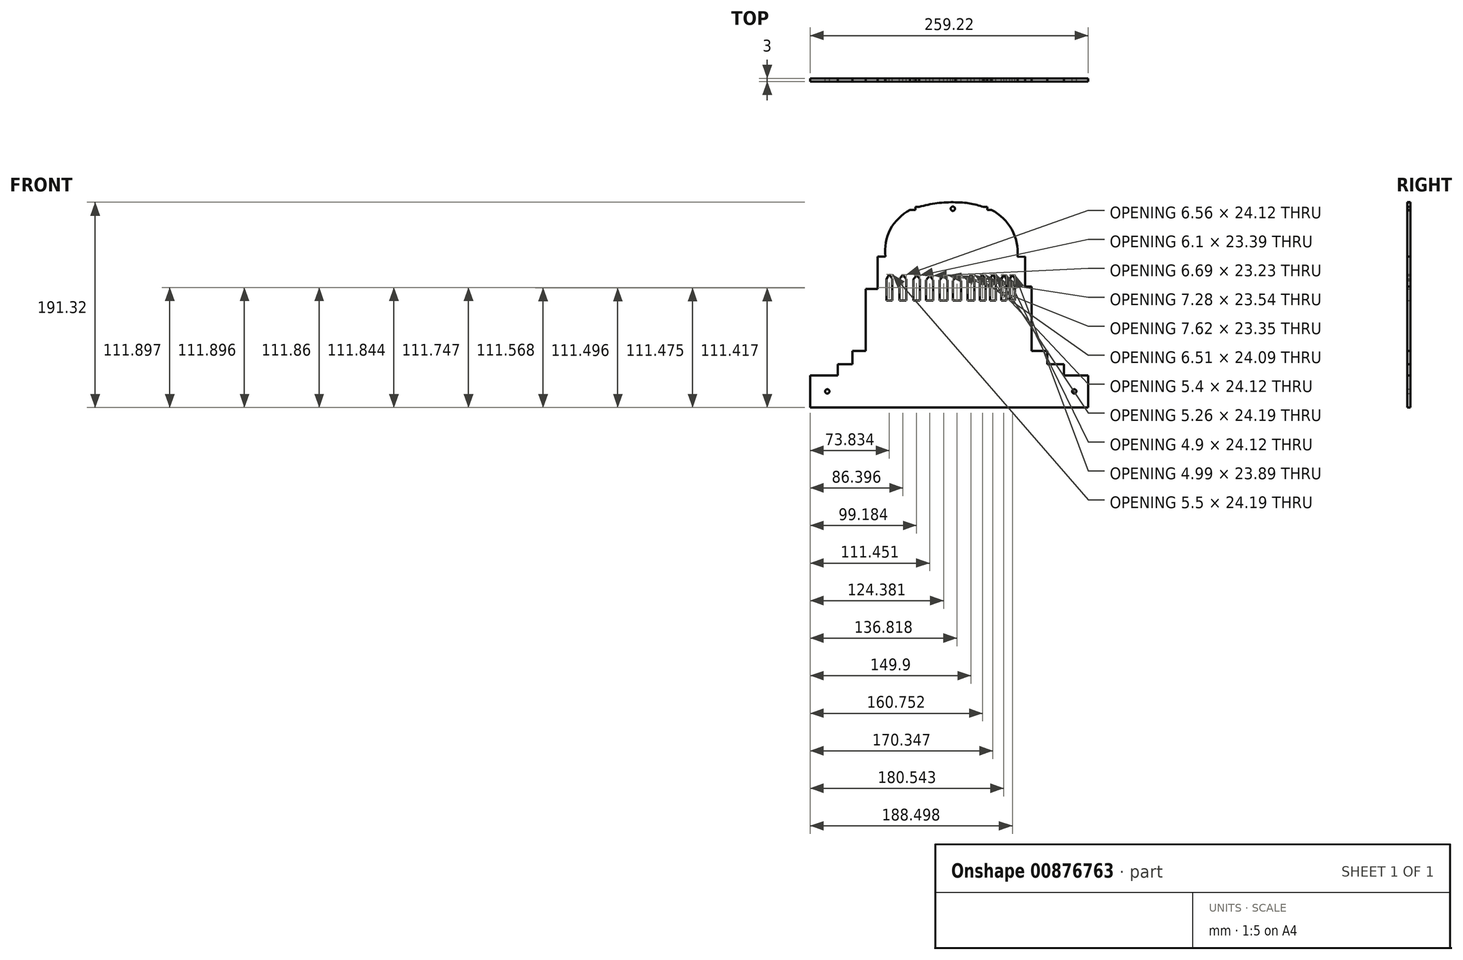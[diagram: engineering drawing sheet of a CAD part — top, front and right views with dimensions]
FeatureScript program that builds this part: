
annotation { "Feature Type Name" : "Feature", "Feature Type Description" : "" }
export const myFeature = defineFeature(function(context is Context, id is Id, definition is map)
    precondition{}
    {
        {
            var Q0;
            Q0=qCreatedBy(makeId("Front.planeOp"),FACE);
            var sketch = newSketch(context, id + "F0", { "sketchPlane" : qUnion([Q0])});
            skLineSegment(sketch, "E0.bottom", {"start": v(-192.48, 145.91) * mm, "end": v(107.52, 145.91) * mm});
            skLineSegment(sketch, "E0.top", {"start": v(-192.48, -54.09) * mm, "end": v(107.52, -54.09) * mm});
            skLineSegment(sketch, "E0.left", {"start": v(-192.48, 145.91) * mm, "end": v(-192.48, -54.09) * mm});
            skLineSegment(sketch, "E0.right", {"start": v(107.52, 145.91) * mm, "end": v(107.52, -54.09) * mm});
            skLineSegment(sketch, "E1.bottom", {"start": v(-179.38, -19.27) * mm, "end": v(79.84, -19.27) * mm});
            skLineSegment(sketch, "E1.top", {"start": v(-179.38, -49.27) * mm, "end": v(79.84, -49.27) * mm});
            skLineSegment(sketch, "E1.left", {"start": v(-179.38, -19.27) * mm, "end": v(-179.38, -49.27) * mm});
            skLineSegment(sketch, "E1.right", {"start": v(79.84, -19.27) * mm, "end": v(79.84, -49.27) * mm});
            skLineSegment(sketch, "E2", {"start": v(-153.49, -19.27) * mm, "end": v(-153.49, -9.07) * mm});
            skLineSegment(sketch, "E3", {"start": v(-153.49, -9.07) * mm, "end": v(57.28, -9.07) * mm});
            skLineSegment(sketch, "E4", {"start": v(57.28, -9.07) * mm, "end": v(57.28, -19.27) * mm});
            skLineSegment(sketch, "E5", {"start": v(-139.9, -9.07) * mm, "end": v(-139.9, 3.53) * mm});
            skLineSegment(sketch, "E6", {"start": v(-139.9, 3.53) * mm, "end": v(41.53, 3.53) * mm});
            skLineSegment(sketch, "E7", {"start": v(41.53, 3.53) * mm, "end": v(41.53, -9.07) * mm});
            skLineSegment(sketch, "E8", {"start": v(27.04, 3.53) * mm, "end": v(27.04, 63.53) * mm});
            skLineSegment(sketch, "E9", {"start": v(-127.6, 3.53) * mm, "end": v(-127.6, 61.2) * mm});
            skLineSegment(sketch, "E10", {"start": v(27.04, 63.53) * mm, "end": v(21.03, 63.53) * mm});
            skLineSegment(sketch, "E11", {"start": v(21.03, 63.53) * mm, "end": v(21.03, 91.26) * mm});
            skLineSegment(sketch, "E12", {"start": v(-116.37, 61.2) * mm, "end": v(-116.37, 91.36) * mm});
            skLineSegment(sketch, "E13", {"start": v(-116.37, 91.36) * mm, "end": v(-109.23, 91.36) * mm});
            skLineSegment(sketch, "E14", {"start": v(-108.3, 50.53) * mm, "end": v(15.5, 50.53) * mm});
            skLineSegment(sketch, "E15", {"start": v(-99.12, 50.53) * mm, "end": v(-99.12, 50.53) * mm});
            skLineSegment(sketch, "E16", {"start": v(-96.27, 50.53) * mm, "end": v(-96.27, 70.4) * mm});
            skLineSegment(sketch, "E17", {"start": v(-89.7, 70.4) * mm, "end": v(-89.7, 50.53) * mm});
            skLineSegment(sketch, "E18", {"start": v(-83.24, 50.53) * mm, "end": v(-83.24, 70.42) * mm});
            skLineSegment(sketch, "E19", {"start": v(-83.24, 70.42) * mm, "end": v(-79.9, 73.92) * mm});
            skLineSegment(sketch, "E20", {"start": v(-79.9, 73.92) * mm, "end": v(-77.15, 70.42) * mm});
            skLineSegment(sketch, "E21", {"start": v(-77.15, 70.42) * mm, "end": v(-77.15, 50.53) * mm});
            skLineSegment(sketch, "E22", {"start": v(-71.27, 50.53) * mm, "end": v(-71.27, 69.55) * mm});
            skLineSegment(sketch, "E23", {"start": v(-71.27, 69.55) * mm, "end": v(-67.9, 73.76) * mm});
            skLineSegment(sketch, "E24", {"start": v(-67.9, 73.76) * mm, "end": v(-64.59, 69.55) * mm});
            skLineSegment(sketch, "E25", {"start": v(-64.59, 69.55) * mm, "end": v(-64.59, 50.53) * mm});
            skLineSegment(sketch, "E26", {"start": v(-58.64, 50.53) * mm, "end": v(-58.64, 69.34) * mm});
            skLineSegment(sketch, "E27", {"start": v(-58.64, 69.34) * mm, "end": v(-54.86, 74.07) * mm});
            skLineSegment(sketch, "E28", {"start": v(-54.86, 74.07) * mm, "end": v(-51.36, 69.34) * mm});
            skLineSegment(sketch, "E29", {"start": v(-51.36, 69.34) * mm, "end": v(-51.36, 50.53) * mm});
            skPoint(sketch, "E30", {"position": v(-54.86, 78.15) * mm});
            skLineSegment(sketch, "E31", {"start": v(-46.37, 50.53) * mm, "end": v(-46.37, 68.7) * mm});
            skLineSegment(sketch, "E32", {"start": v(-46.37, 68.7) * mm, "end": v(-42.4, 73.88) * mm});
            skLineSegment(sketch, "E33", {"start": v(-42.4, 73.88) * mm, "end": v(-38.75, 68.7) * mm});
            skLineSegment(sketch, "E34", {"start": v(-38.75, 68.7) * mm, "end": v(-38.75, 50.53) * mm});
            skLineSegment(sketch, "E35", {"start": v(-32.74, 50.53) * mm, "end": v(-32.74, 69.57) * mm});
            skLineSegment(sketch, "E36", {"start": v(-32.74, 69.57) * mm, "end": v(-29.58, 74.62) * mm});
            skLineSegment(sketch, "E37", {"start": v(-29.58, 74.62) * mm, "end": v(-26.22, 69.57) * mm});
            skLineSegment(sketch, "E38", {"start": v(-26.22, 69.57) * mm, "end": v(-26.22, 50.53) * mm});
            skPoint(sketch, "E39.start.orphan", {"position": v(-7.93, 138.52) * mm});
            skLineSegment(sketch, "E40", {"start": v(21.03, 91.26) * mm, "end": v(-7.93, 91) * mm});
            skLineSegment(sketch, "E41", {"start": v(-96.27, 70.4) * mm, "end": v(-93, 74.65) * mm});
            skLineSegment(sketch, "E42", {"start": v(-89.7, 70.4) * mm, "end": v(-93, 74.65) * mm});
            skLineSegment(sketch, "E43", {"start": v(-21.33, 50.53) * mm, "end": v(-21.33, 70.4) * mm});
            skLineSegment(sketch, "E44", {"start": v(-21.33, 70.4) * mm, "end": v(-18.98, 74.65) * mm});
            skLineSegment(sketch, "E45", {"start": v(-18.98, 74.65) * mm, "end": v(-15.93, 70.4) * mm});
            skLineSegment(sketch, "E46", {"start": v(-15.93, 70.4) * mm, "end": v(-15.93, 50.53) * mm});
            skLineSegment(sketch, "E47", {"start": v(-1.29, 50.53) * mm, "end": v(-1.29, 70.4) * mm});
            skLineSegment(sketch, "E48", {"start": v(-1.29, 70.4) * mm, "end": v(1.29, 74.65) * mm});
            skLineSegment(sketch, "E49", {"start": v(1.29, 74.65) * mm, "end": v(3.61, 70.4) * mm});
            skLineSegment(sketch, "E50", {"start": v(3.61, 70.4) * mm, "end": v(3.61, 50.53) * mm});
            skLineSegment(sketch, "E51", {"start": v(-11.66, 50.53) * mm, "end": v(-11.66, 70.4) * mm});
            skLineSegment(sketch, "E52", {"start": v(-6.4, 70.4) * mm, "end": v(-6.4, 50.53) * mm});
            skLineSegment(sketch, "E53", {"start": v(-109.23, 91.36) * mm, "end": v(-7.93, 91) * mm});
            skLineSegment(sketch, "E54", {"start": v(-11.66, 70.4) * mm, "end": v(-9.13, 74.72) * mm});
            skLineSegment(sketch, "E55", {"start": v(-9.13, 74.72) * mm, "end": v(-6.4, 70.4) * mm});
            skLineSegment(sketch, "E56", {"start": v(6.63, 50.53) * mm, "end": v(6.63, 70.47) * mm});
            skLineSegment(sketch, "E57", {"start": v(6.63, 70.47) * mm, "end": v(8.86, 74.42) * mm});
            skLineSegment(sketch, "E58", {"start": v(8.86, 74.42) * mm, "end": v(11.61, 70.7) * mm});
            skLineSegment(sketch, "E59", {"start": v(11.61, 70.7) * mm, "end": v(11.61, 50.53) * mm});
            skLineSegment(sketch, "E60", {"start": v(15.5, 50.53) * mm, "end": v(21.03, 63.53) * mm});
            skArc(sketch, "E61", {"start": v(13.96, 91.2) * mm, "mid": v(8.52, 116.74) * mm, "end": v(-10.34, 134.8) * mm});
            skArc(sketch, "E62", {"start": v(-86.27, 134.8) * mm, "mid": v(-104.6, 116.7) * mm, "end": v(-109.23, 91.36) * mm});
            skLineSegment(sketch, "E63", {"start": v(-127.6, 61.2) * mm, "end": v(-116.37, 61.2) * mm});
            skLineSegment(sketch, "E64", {"start": v(-116.37, 61.2) * mm, "end": v(-108.3, 50.53) * mm});
            skPoint(sketch, "E65.orphan", {"position": v(-116.37, 50.53) * mm});
            skLineSegment(sketch, "E66", {"start": v(-108.3, 50.53) * mm, "end": v(-108.3, 70.5) * mm});
            skLineSegment(sketch, "E67", {"start": v(-108.3, 70.5) * mm, "end": v(-105.84, 74.72) * mm});
            skLineSegment(sketch, "E68", {"start": v(-105.84, 74.72) * mm, "end": v(-102.8, 70.7) * mm});
            skLineSegment(sketch, "E69", {"start": v(-102.8, 70.7) * mm, "end": v(-102.8, 50.53) * mm});
            skLineSegment(sketch, "E70", {"start": v(-86.27, 134.8) * mm, "end": v(-81.18, 134.8) * mm});
            skLineSegment(sketch, "E71", {"start": v(-81.18, 134.8) * mm, "end": v(-81.18, 137.64) * mm});
            skLineSegment(sketch, "E72", {"start": v(-14.26, 137.64) * mm, "end": v(-14.26, 134.8) * mm});
            skArc(sketch, "E73", {"start": v(-43.97, 141.98) * mm, "mid": v(-61.1, 141.2) * mm, "end": v(-77.85, 137.64) * mm});
            skArc(sketch, "E74", {"start": v(-17.8, 137.64) * mm, "mid": v(-30.7, 140.97) * mm, "end": v(-43.97, 141.98) * mm});
            skLineSegment(sketch, "E75.trimOffspring", {"start": v(-14.26, 134.8) * mm, "end": v(-10.34, 134.8) * mm});
            skLineSegment(sketch, "E76", {"start": v(-81.18, 137.64) * mm, "end": v(-77.85, 137.64) * mm});
            skLineSegment(sketch, "E77", {"start": v(-14.26, 137.64) * mm, "end": v(-17.8, 137.64) * mm});
            skCircle(sketch, "E78", {"center": v(-163.38, -34.27) * mm, "radius": 2 * mm});
            skCircle(sketch, "E79", {"center": v(66.84, -34.27) * mm, "radius": 2 * mm});
            skCircle(sketch, "E80", {"center": v(-46.38, 136.03) * mm, "radius": 2 * mm});
            skSolve(sketch);
        }
        {
            var Q0;
            {var subQ16=sQuery(id+"F0.wireOp",EDGE,"E11");Q0=makeQuery(id+"F0.imprint","IMPRINT",FACE,{"disambiguationData":[TD([[makeQuery(id+"F0.imprint","IMPRINT",EDGE,{"derivedFrom":subQ16}),1.0]])]});}
            var Q1;
            {var subQ0=sQuery(id+"F0.wireOp",EDGE,"E53");Q1=makeQuery(id+"F0.imprint","IMPRINT",FACE,{"disambiguationData":[TD([[makeQuery(id+"F0.imprint","IMPRINT",EDGE,{"derivedFrom":subQ0}),1.0]])]});}
            var Q2;
            {var subQ15=sQuery(id+"F0.wireOp",EDGE,"E8");Q2=makeQuery(id+"F0.imprint","IMPRINT",FACE,{"disambiguationData":[TD([[makeQuery(id+"F0.imprint","IMPRINT",EDGE,{"derivedFrom":subQ15}),1.0]])]});}
            var Q3;
            {var subQ3=sQuery(id+"F0.wireOp",EDGE,"E2");Q3=makeQuery(id+"F0.imprint","IMPRINT",FACE,{"disambiguationData":[TD([[makeQuery(id+"F0.imprint","IMPRINT",EDGE,{"derivedFrom":subQ3}),-1.0]])]});}
            var Q4;
            {var subQ1=sQuery(id+"F0.wireOp",EDGE,"E5");Q4=makeQuery(id+"F0.imprint","IMPRINT",FACE,{"disambiguationData":[TD([[makeQuery(id+"F0.imprint","IMPRINT",EDGE,{"derivedFrom":subQ1}),-1.0]])]});}
            var Q5;
            Q5=makeQuery(id+"F0.imprint","IMPRINT",FACE,{"disambiguationData":[TD([[makeQuery(id+"F0.imprint","IMPRINT",EDGE,{"derivedFrom":sQuery(id+"F0.wireOp",EDGE,"E1.top")}),1.0]])]});
            extrude(context, id + "F1", {"entities" : qUnion([Q0, Q1, Q2, Q3, Q4, Q5]), "depth" : 3 * mm, "offsetDistance" : 25 * mm});
        }
    });
